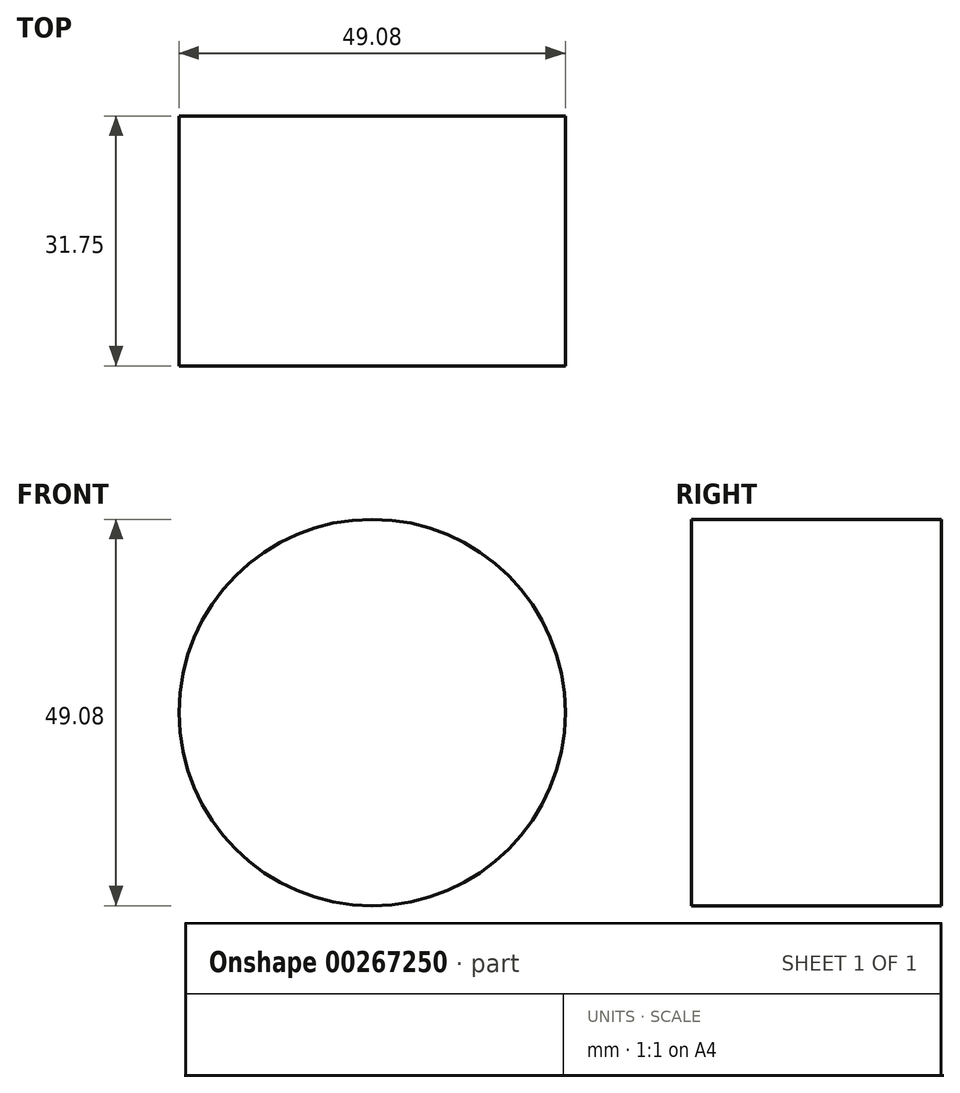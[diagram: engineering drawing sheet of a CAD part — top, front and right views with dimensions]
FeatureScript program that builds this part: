
annotation { "Feature Type Name" : "Feature", "Feature Type Description" : "" }
export const myFeature = defineFeature(function(context is Context, id is Id, definition is map)
    precondition{}
    {
        {
            var Q0;
            Q0=qCreatedBy(makeId("Front.planeOp"),FACE);
            var sketch = newSketch(context, id + "F0", { "sketchPlane" : qUnion([Q0])});
            skCircle(sketch, "E0", {"center": v(0, 0) * mm, "radius": 24.54 * mm});
            skSolve(sketch);
        }
        {
            var Q0;
            Q0=makeQuery(id+"F0.imprint","IMPRINT",FACE,{"disambiguationData":[TD([[makeQuery(id+"F0.imprint","IMPRINT",EDGE,{"derivedFrom":sQuery(id+"F0.wireOp",EDGE,"E0")}),1.0]])]});
            extrude(context, id + "F1", {"entities" : qUnion([Q0]), "depth" : 31.75 * mm});
        }
    });
